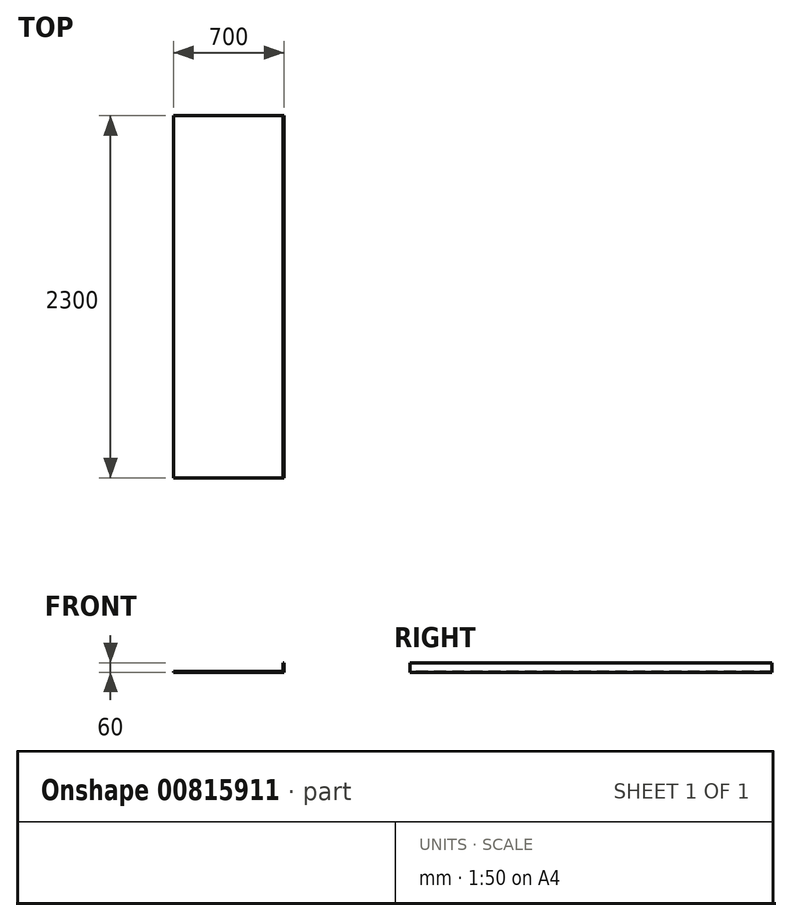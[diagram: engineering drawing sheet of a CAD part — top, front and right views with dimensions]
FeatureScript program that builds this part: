
annotation { "Feature Type Name" : "Feature", "Feature Type Description" : "" }
export const myFeature = defineFeature(function(context is Context, id is Id, definition is map)
    precondition{}
    {
        {
            var Q0;
            Q0=qCreatedBy(makeId("Front.planeOp"),FACE);
            var sketch = newSketch(context, id + "F0", { "sketchPlane" : qUnion([Q0])});
            skLineSegment(sketch, "E0", {"start": v(0, 0) * mm, "end": v(700, 0) * mm});
            skLineSegment(sketch, "E1", {"start": v(700, 0) * mm, "end": v(700, 60) * mm});
            skLineSegment(sketch, "E2.0", {"start": v(696, 4) * mm, "end": v(696, 60) * mm});
            skLineSegment(sketch, "E2.1", {"start": v(0, 4) * mm, "end": v(696, 4) * mm});
            skLineSegment(sketch, "E3", {"start": v(0, 0) * mm, "end": v(0, 4) * mm});
            skLineSegment(sketch, "E4", {"start": v(696, 60) * mm, "end": v(700, 60) * mm});
            skSolve(sketch);
        }
        {
            var Q0;
            Q0=qSketchRegion(id+"F0",true);
            extrude(context, id + "F1", {"entities" : qUnion([Q0]), "oppositeDirection" : true, "depth" : 2300 * mm, "offsetDistance" : 25.4 * mm});
        }
    });
